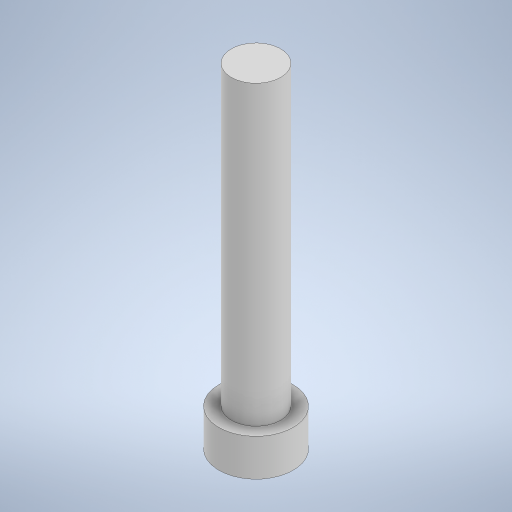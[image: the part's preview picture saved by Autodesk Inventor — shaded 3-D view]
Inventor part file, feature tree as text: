
AUTODESK INVENTOR PART (.ipt)
format: ipt  version: 2024.2 (Build 282272000, 272)  size: 237,056 bytes
history: native  units: mm
features: extrude x2, sketch x2
ambient origin geometry x8: Origin, YZ Plane, XZ Plane, XY Plane, X Axis, Y Axis, Z Axis, Center Point
bodies: Solid1 (feature_tree)
feature tree (4):
  extrude  "Extrusion1"  Depth=1.5mm TaperAngle=0.0deg
  extrude  "Extrusion2"  Depth=12.0mm TaperAngle=0.0deg
  sketch  "Sketch1"  dims[d0=3.0mm d1=1.5mm d2=0.0mm]
  sketch  "Sketch2"  dims[d3=2.0mm d4=12.0mm d5=0.0mm]
